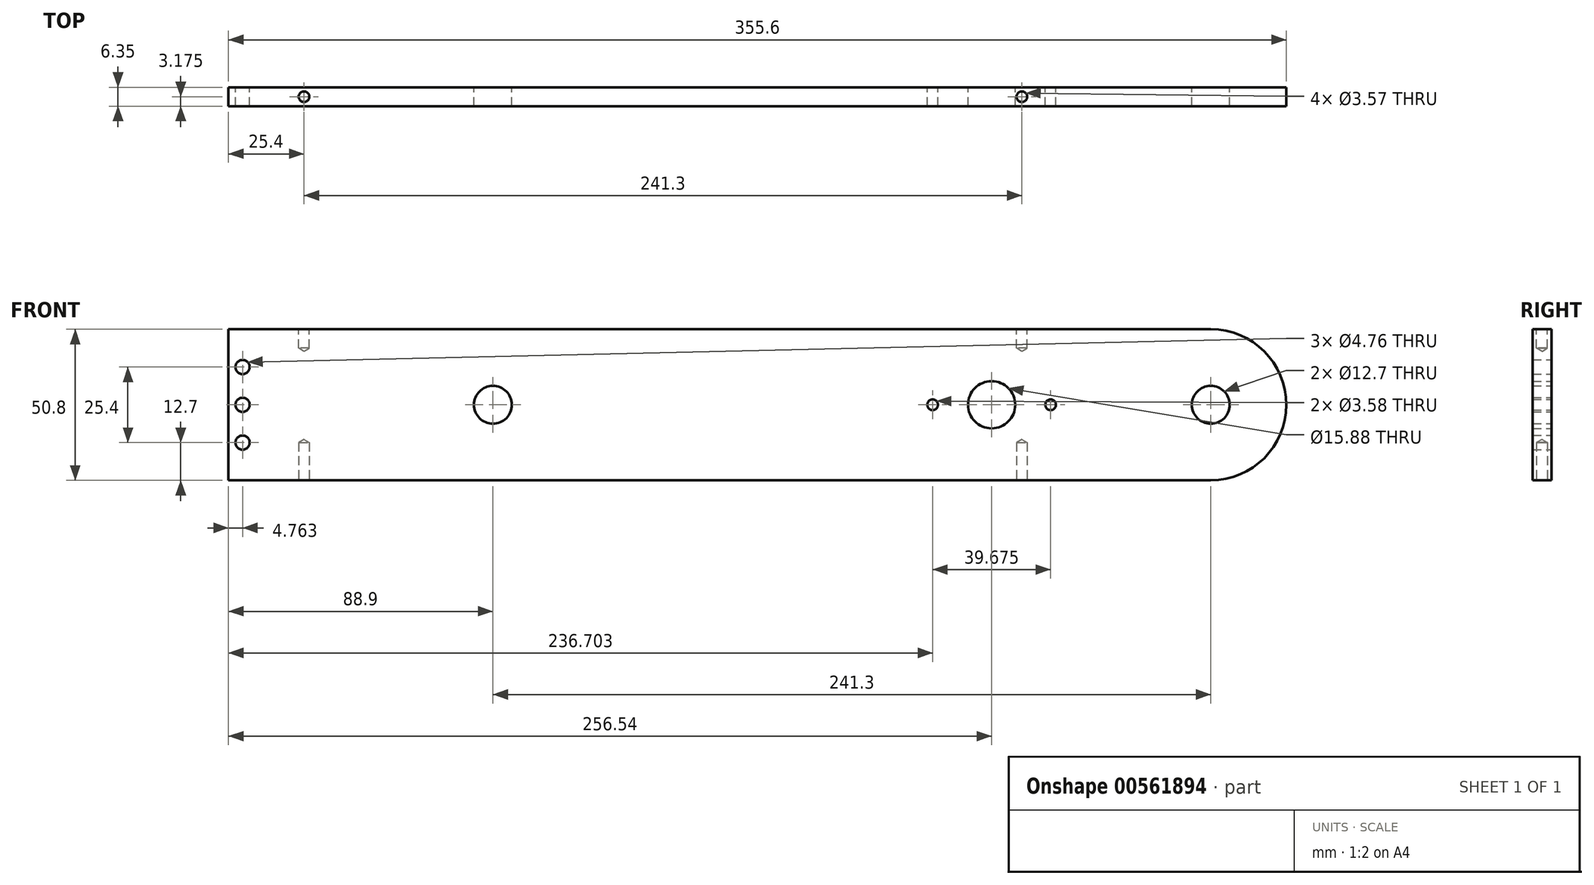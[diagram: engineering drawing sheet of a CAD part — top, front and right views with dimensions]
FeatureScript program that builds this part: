
annotation { "Feature Type Name" : "Feature", "Feature Type Description" : "" }
export const myFeature = defineFeature(function(context is Context, id is Id, definition is map)
    precondition{}
    {
        {
            var Q0;
            Q0=qCreatedBy(makeId("Front.planeOp"),FACE);
            var sketch = newSketch(context, id + "F0", { "sketchPlane" : qUnion([Q0])});
            skLineSegment(sketch, "E0", {"start": v(0, 0) * mm, "end": v(330.2, 0) * mm});
            skLineSegment(sketch, "E1", {"start": v(330.2, 50.8) * mm, "end": v(0, 50.8) * mm});
            skLineSegment(sketch, "E2", {"start": v(0, 50.8) * mm, "end": v(0, 0) * mm});
            skArc(sketch, "E3", {"start": v(330.2, 0) * mm, "mid": v(355.6, 25.4) * mm, "end": v(330.2, 50.8) * mm});
            skCircle(sketch, "E4", {"center": v(330.2, 25.4) * mm, "radius": 6.35 * mm});
            skCircle(sketch, "E5", {"center": v(88.9, 25.4) * mm, "radius": 6.35 * mm});
            skLineSegment(sketch, "E6", {"start": v(330.2, 50.8) * mm, "end": v(355.6, 50.8) * mm, "construction": true});
            skLineSegment(sketch, "E7", {"start": v(355.6, 50.8) * mm, "end": v(355.6, 0) * mm, "construction": true});
            skLineSegment(sketch, "E8", {"start": v(355.6, 0) * mm, "end": v(330.2, 0) * mm, "construction": true});
            skCircle(sketch, "E9", {"center": v(88.9, 25.4) * mm, "radius": 19.43 * mm, "construction": true});
            skCircle(sketch, "E10", {"center": v(256.54, 25.4) * mm, "radius": 19.43 * mm, "construction": true});
            skLineSegment(sketch, "E11", {"start": v(90.14, 6) * mm, "end": v(257.78, 6) * mm, "construction": true});
            skLineSegment(sketch, "E12", {"start": v(88.15, 44.82) * mm, "end": v(256.54, 44.83) * mm, "construction": true});
            skCircle(sketch, "E13", {"center": v(256.54, 25.4) * mm, "radius": 7.94 * mm});
            skPoint(sketch, "E14.endSnap0", {"position": v(0, 25.4) * mm});
            skPoint(sketch, "E15", {"position": v(4.76, 25.4) * mm});
            skPoint(sketch, "E16", {"position": v(4.76, 38.1) * mm});
            skPoint(sketch, "E17", {"position": v(4.76, 12.7) * mm});
            skLineSegment(sketch, "E18", {"start": v(330.2, 25.4) * mm, "end": v(256.54, 25.4) * mm, "construction": true});
            skLineSegment(sketch, "E19", {"start": v(293.37, 25.4) * mm, "end": v(293.37, 50.8) * mm, "construction": true});
            skPoint(sketch, "E20", {"position": v(0, 50.8) * mm});
            skPoint(sketch, "E21", {"position": v(330.2, 50.8) * mm});
            skLineSegment(sketch, "E22", {"start": v(256.54, 25.4) * mm, "end": v(236.7, 25.4) * mm, "construction": true});
            skLineSegment(sketch, "E23", {"start": v(256.54, 25.4) * mm, "end": v(276.38, 25.4) * mm});
            skCircle(sketch, "E24", {"center": v(236.7, 25.4) * mm, "radius": 1.8 * mm});
            skCircle(sketch, "E25", {"center": v(276.38, 25.4) * mm, "radius": 1.8 * mm});
            skSolve(sketch);
        }
        {
            var Q0;
            Q0 = qSketchRegion(id + "F0", true);
            extrude(context, id + "F1", {"entities" : qUnion([Q0]), "depth" : 6.35 * mm, "offsetDistance" : 25.4 * mm});
        }
        {
            var Q0;
            Q0=sQuery(id+"F0.wireOp",VERTEX,"E15");
            var Q1;
            Q1=makeQuery(id+"F1.opExtrude","SWEPT_BODY",BODY,{"disambiguationData":[OSD([sQuery(id+"F0.wireOp",EDGE,"E0"),sQuery(id+"F0.wireOp",EDGE,"E1"),sQuery(id+"F0.wireOp",EDGE,"E2"),sQuery(id+"F0.wireOp",EDGE,"E3"),sQuery(id+"F0.wireOp",EDGE,"E4"),sQuery(id+"F0.wireOp",EDGE,"E5"),sQuery(id+"F0.wireOp",EDGE,"E13")])]});
            hole(context, id + "F2", {"style" : HoleStyle.SIMPLE, "endStyle" : HoleEndStyle.BLIND, "oppositeDirection" : true, "holeDiameter" : 4.76 * mm, "majorDiameter" : 6.35 * mm, "holeDepth" : 12.7 * mm, "isTappedThrough" : true, "tappedDepth" : 12.7 * mm, "tapClearance" : 3, "startFromSketch" : true, "locations" : qUnion([Q0]), "scope" : qUnion([Q1])});
        }
        {
            var Q0;
            Q0=sQuery(id+"F0.wireOp",VERTEX,"E17");
            var Q1;
            Q1=makeQuery(id+"F1.opExtrude","SWEPT_BODY",BODY,{"disambiguationData":[OSD([sQuery(id+"F0.wireOp",EDGE,"E0"),sQuery(id+"F0.wireOp",EDGE,"E1"),sQuery(id+"F0.wireOp",EDGE,"E2"),sQuery(id+"F0.wireOp",EDGE,"E3"),sQuery(id+"F0.wireOp",EDGE,"E4"),sQuery(id+"F0.wireOp",EDGE,"E5"),sQuery(id+"F0.wireOp",EDGE,"E13")])]});
            hole(context, id + "F3", {"style" : HoleStyle.SIMPLE, "endStyle" : HoleEndStyle.BLIND, "oppositeDirection" : true, "holeDiameter" : 4.76 * mm, "majorDiameter" : 6.35 * mm, "holeDepth" : 12.7 * mm, "isTappedThrough" : true, "tappedDepth" : 12.7 * mm, "tapClearance" : 3, "startFromSketch" : true, "locations" : qUnion([Q0]), "scope" : qUnion([Q1])});
        }
        {
            var Q0;
            Q0=sQuery(id+"F0.wireOp",VERTEX,"E16");
            var Q1;
            Q1=makeQuery(id+"F1.opExtrude","SWEPT_BODY",BODY,{"disambiguationData":[OSD([sQuery(id+"F0.wireOp",EDGE,"E0"),sQuery(id+"F0.wireOp",EDGE,"E1"),sQuery(id+"F0.wireOp",EDGE,"E2"),sQuery(id+"F0.wireOp",EDGE,"E3"),sQuery(id+"F0.wireOp",EDGE,"E4"),sQuery(id+"F0.wireOp",EDGE,"E5"),sQuery(id+"F0.wireOp",EDGE,"E13")])]});
            hole(context, id + "F4", {"style" : HoleStyle.SIMPLE, "endStyle" : HoleEndStyle.BLIND, "oppositeDirection" : true, "holeDiameter" : 4.76 * mm, "majorDiameter" : 6.35 * mm, "holeDepth" : 12.7 * mm, "isTappedThrough" : true, "tappedDepth" : 12.7 * mm, "tapClearance" : 3, "startFromSketch" : true, "locations" : qUnion([Q0]), "scope" : qUnion([Q1])});
        }
        {
            var Q0;
            Q0=qCreatedBy(makeId("Top.planeOp"),FACE);
            var sketch = newSketch(context, id + "F5", { "sketchPlane" : qUnion([Q0])});
            skLineSegment(sketch, "E26.bottom", {"start": v(0, -6.35) * mm, "end": v(330.2, -6.35) * mm, "construction": true});
            skLineSegment(sketch, "E26.top", {"start": v(0, 0) * mm, "end": v(330.2, 0) * mm, "construction": true});
            skLineSegment(sketch, "E26.left", {"start": v(0, -6.35) * mm, "end": v(0, 0) * mm, "construction": true});
            skLineSegment(sketch, "E26.right", {"start": v(330.2, -6.35) * mm, "end": v(330.2, 0) * mm, "construction": true});
            skLineSegment(sketch, "E27", {"start": v(330.2, -3.18) * mm, "end": v(266.7, -3.18) * mm, "construction": true});
            skPoint(sketch, "E28", {"position": v(266.7, -3.18) * mm});
            skLineSegment(sketch, "E29", {"start": v(0, -3.18) * mm, "end": v(25.4, -3.18) * mm, "construction": true});
            skPoint(sketch, "E30", {"position": v(25.4, -3.18) * mm});
            skLineSegment(sketch, "E31", {"start": v(330.2, -3.18) * mm, "end": v(266.7, -3.18) * mm});
            skSolve(sketch);
        }
        {
            var Q0;
            Q0=sQuery(id+"F5.wireOp",VERTEX,"E28");
            var Q1;
            Q1=makeQuery(id+"F1.opExtrude","SWEPT_BODY",BODY,{"disambiguationData":[OSD([sQuery(id+"F0.wireOp",EDGE,"E0"),sQuery(id+"F0.wireOp",EDGE,"E1"),sQuery(id+"F0.wireOp",EDGE,"E2"),sQuery(id+"F0.wireOp",EDGE,"E3"),sQuery(id+"F0.wireOp",EDGE,"E4"),sQuery(id+"F0.wireOp",EDGE,"E5"),sQuery(id+"F0.wireOp",EDGE,"E13")])]});
            hole(context, id + "F6", {"style" : HoleStyle.SIMPLE, "endStyle" : HoleEndStyle.BLIND, "oppositeDirection" : true, "holeDiameter" : 3.57 * mm, "majorDiameter" : 6.35 * mm, "holeDepth" : 12.7 * mm, "isTappedThrough" : true, "tappedDepth" : 12.7 * mm, "tapClearance" : 3, "startFromSketch" : true, "locations" : qUnion([Q0]), "scope" : qUnion([Q1])});
        }
        {
            var Q0;
            Q0=sQuery(id+"F5.wireOp",VERTEX,"E30");
            var Q1;
            Q1=makeQuery(id+"F1.opExtrude","SWEPT_BODY",BODY,{"disambiguationData":[OSD([sQuery(id+"F0.wireOp",EDGE,"E0"),sQuery(id+"F0.wireOp",EDGE,"E1"),sQuery(id+"F0.wireOp",EDGE,"E2"),sQuery(id+"F0.wireOp",EDGE,"E3"),sQuery(id+"F0.wireOp",EDGE,"E4"),sQuery(id+"F0.wireOp",EDGE,"E5"),sQuery(id+"F0.wireOp",EDGE,"E13")])]});
            hole(context, id + "F7", {"style" : HoleStyle.SIMPLE, "endStyle" : HoleEndStyle.BLIND, "oppositeDirection" : true, "holeDiameter" : 3.57 * mm, "majorDiameter" : 6.35 * mm, "holeDepth" : 12.7 * mm, "isTappedThrough" : true, "tappedDepth" : 12.7 * mm, "tapClearance" : 3, "startFromSketch" : true, "locations" : qUnion([Q0]), "scope" : qUnion([Q1])});
        }
        {
            var Q0;
            Q0=makeQuery(id+"F1.opExtrude","SWEPT_FACE",FACE,{"disambiguationData":[OSD([sQuery(id+"F0.wireOp",EDGE,"E1")])]});
            var sketch = newSketch(context, id + "F8", { "sketchPlane" : qUnion([Q0])});
            skLineSegment(sketch, "E32.bottom", {"start": v(0, 0) * mm, "end": v(330.2, 0) * mm, "construction": true});
            skLineSegment(sketch, "E32.top", {"start": v(0, -6.35) * mm, "end": v(330.2, -6.35) * mm, "construction": true});
            skLineSegment(sketch, "E32.left", {"start": v(0, 0) * mm, "end": v(0, -6.35) * mm, "construction": true});
            skLineSegment(sketch, "E32.right", {"start": v(330.2, 0) * mm, "end": v(330.2, -6.35) * mm, "construction": true});
            skLineSegment(sketch, "E33", {"start": v(0, -3.18) * mm, "end": v(25.4, -3.18) * mm, "construction": true});
            skLineSegment(sketch, "E34", {"start": v(330.2, -3.18) * mm, "end": v(266.7, -3.18) * mm, "construction": true});
            skSolve(sketch);
        }
        {
            var Q0;
            Q0=sQuery(id+"F8.wireOp",VERTEX,"E34.end");
            var Q1;
            Q1=makeQuery(id+"F1.opExtrude","SWEPT_BODY",BODY,{"disambiguationData":[OSD([sQuery(id+"F0.wireOp",EDGE,"E0"),sQuery(id+"F0.wireOp",EDGE,"E1"),sQuery(id+"F0.wireOp",EDGE,"E2"),sQuery(id+"F0.wireOp",EDGE,"E3"),sQuery(id+"F0.wireOp",EDGE,"E4"),sQuery(id+"F0.wireOp",EDGE,"E5"),sQuery(id+"F0.wireOp",EDGE,"E13")])]});
            hole(context, id + "F9", {"style" : HoleStyle.SIMPLE, "endStyle" : HoleEndStyle.BLIND, "holeDiameter" : 3.57 * mm, "majorDiameter" : 6.35 * mm, "holeDepth" : 6.35 * mm, "isTappedThrough" : true, "tappedDepth" : 12.7 * mm, "tapClearance" : 3, "startFromSketch" : true, "locations" : qUnion([Q0]), "scope" : qUnion([Q1])});
        }
        {
            var Q0;
            Q0=sQuery(id+"F8.wireOp",VERTEX,"E33.end");
            var Q1;
            Q1=makeQuery(id+"F1.opExtrude","SWEPT_BODY",BODY,{"disambiguationData":[OSD([sQuery(id+"F0.wireOp",EDGE,"E0"),sQuery(id+"F0.wireOp",EDGE,"E1"),sQuery(id+"F0.wireOp",EDGE,"E2"),sQuery(id+"F0.wireOp",EDGE,"E3"),sQuery(id+"F0.wireOp",EDGE,"E4"),sQuery(id+"F0.wireOp",EDGE,"E5"),sQuery(id+"F0.wireOp",EDGE,"E13")])]});
            hole(context, id + "F10", {"style" : HoleStyle.SIMPLE, "endStyle" : HoleEndStyle.BLIND, "holeDiameter" : 3.57 * mm, "majorDiameter" : 6.35 * mm, "holeDepth" : 6.35 * mm, "isTappedThrough" : true, "tappedDepth" : 12.7 * mm, "tapClearance" : 3, "startFromSketch" : true, "locations" : qUnion([Q0]), "scope" : qUnion([Q1])});
        }
    });
